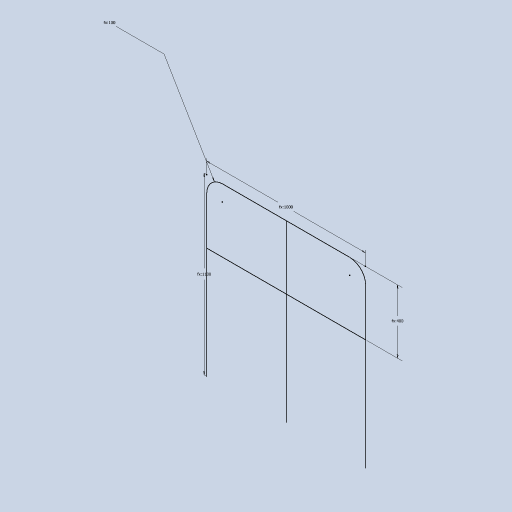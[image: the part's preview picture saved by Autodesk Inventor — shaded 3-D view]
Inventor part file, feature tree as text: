
AUTODESK INVENTOR PART (.ipt)
format: ipt  version: 2024.3 (Build 283343000, 343)  size: 84,480 bytes
history: native  units: mm
features: sketch x1
ambient origin geometry x8: Origin, YZ Plane, XZ Plane, XY Plane, X Axis, Y Axis, Z Axis, Center Point
feature tree (1):
  sketch  "Sketch4"  dims[d25=1100.0mm d26=1000.0mm d27=100.0mm]
